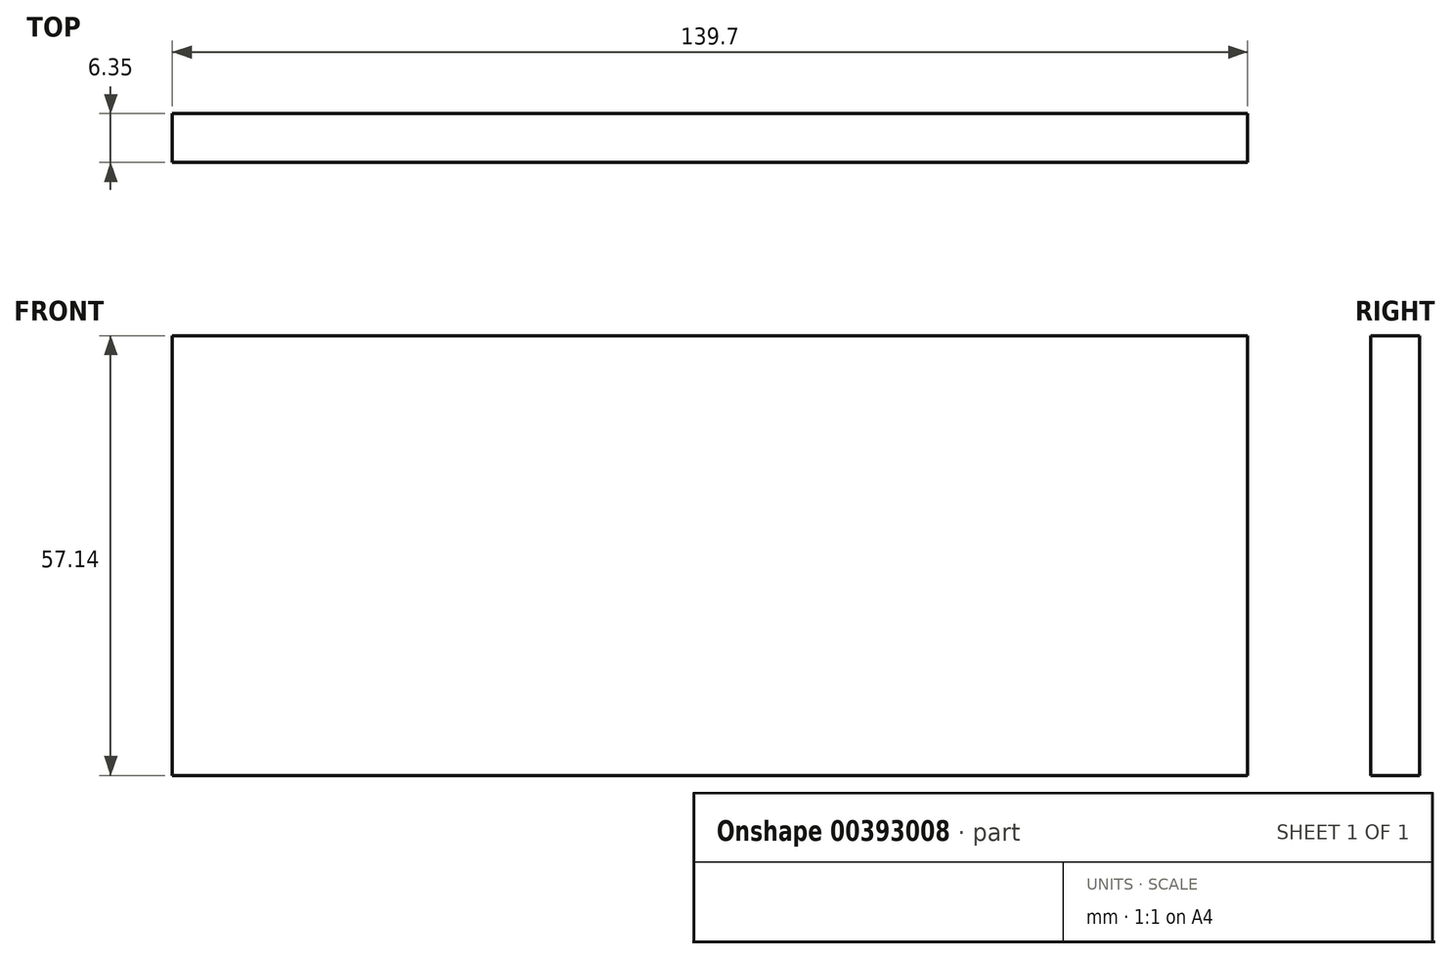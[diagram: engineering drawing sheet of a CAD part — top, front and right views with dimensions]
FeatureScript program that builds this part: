
annotation { "Feature Type Name" : "Feature", "Feature Type Description" : "" }
export const myFeature = defineFeature(function(context is Context, id is Id, definition is map)
    precondition{}
    {
        {
            var Q0;
            Q0=qCreatedBy(makeId("Front.planeOp"),FACE);
            var sketch = newSketch(context, id + "F0", { "sketchPlane" : qUnion([Q0])});
            skLineSegment(sketch, "E0.bottom", {"start": v(69.85, -28.58) * mm, "end": v(-69.85, -28.58) * mm});
            skLineSegment(sketch, "E0.top", {"start": v(69.85, 28.58) * mm, "end": v(-69.85, 28.58) * mm});
            skLineSegment(sketch, "E0.left", {"start": v(69.85, -28.58) * mm, "end": v(69.85, 28.57) * mm});
            skLineSegment(sketch, "E0.right", {"start": v(-69.85, -28.58) * mm, "end": v(-69.85, 28.57) * mm});
            skPoint(sketch, "E0.middle", {"position": v(0, 0) * mm});
            skSolve(sketch);
        }
        {
            var Q0;
            Q0=qSketchRegion(id+"F0",true);
            extrude(context, id + "F1", {"entities" : qUnion([Q0]), "depth" : 6.35 * mm});
        }
    });
